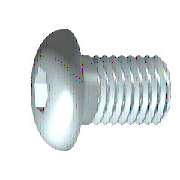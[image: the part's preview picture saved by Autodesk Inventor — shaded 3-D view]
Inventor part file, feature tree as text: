
AUTODESK INVENTOR PART (.ipt)
format: ipt  version: 2024.1 (Build 281209000, 209)  size: 207,872 bytes
history: native  units: mm (DEFAULTED — no unit token found)
features: extrude x1, plane x1, fillet x1, thread x1
ambient origin geometry x7: Origin, YZ Plane, XY Plane, X Axis, Y Axis, Z Axis, Center Point
bodies: Solid1 (feature_tree), Body (feature_tree)
feature tree (4):
  extrude  "Slot"  Depth=3.0mm
  plane  "Work Plane1"
  fillet  "Fillet2"  Radius=0.306825mm
  thread  "Thread2"  [1 undecoded]
note: 1 required parameter value undecoded (feature->parameter linkage not recoverable at this tier; creation-order binding heuristic only, values carry confidence <= 0.55)
